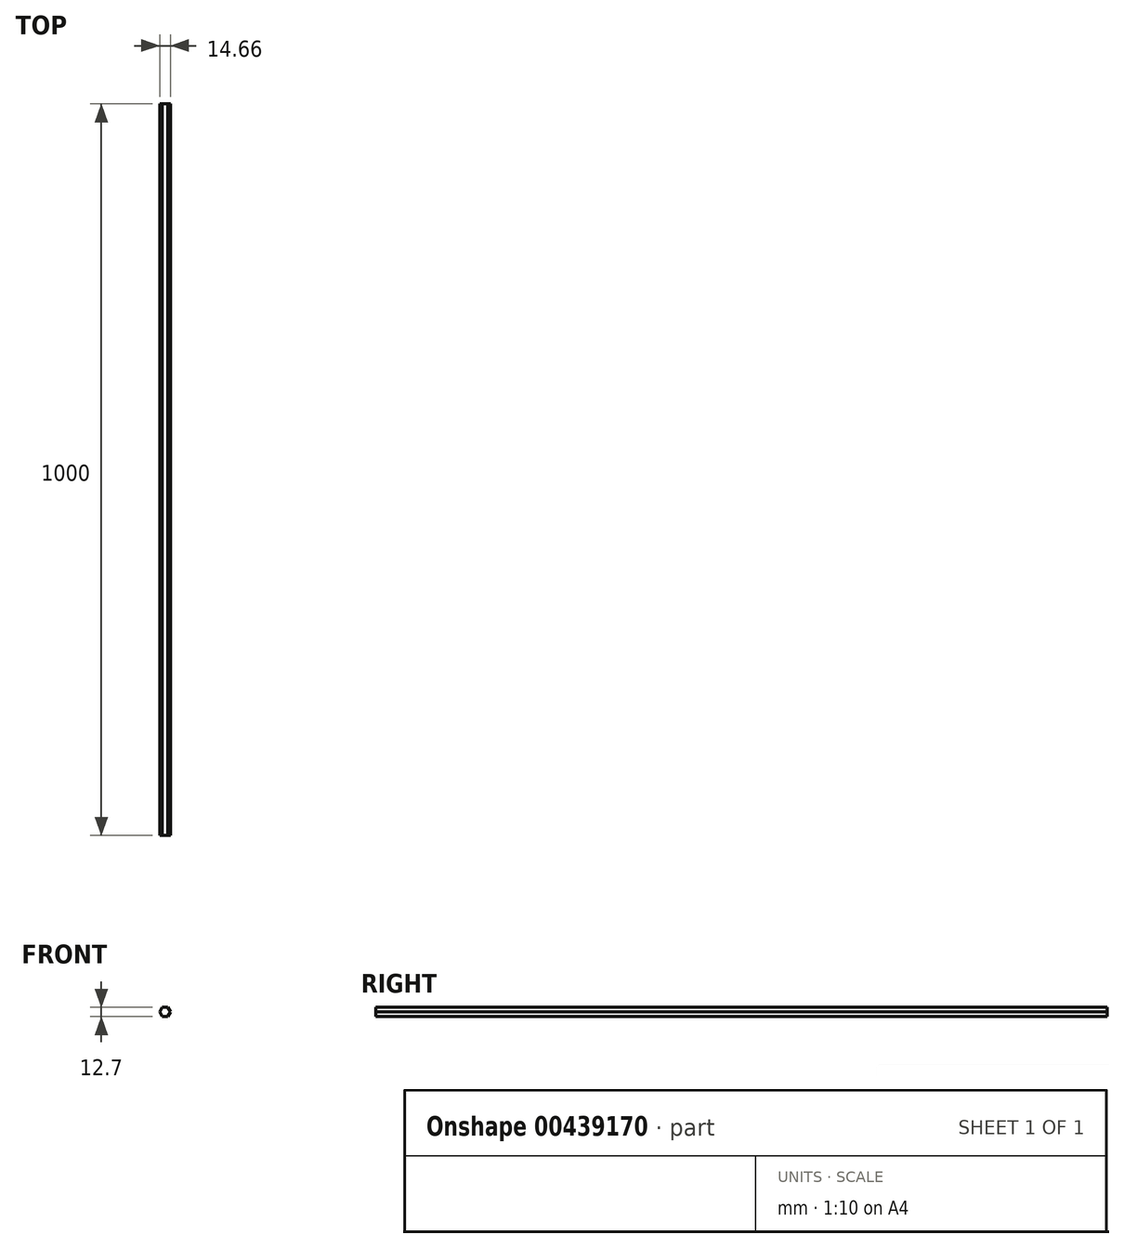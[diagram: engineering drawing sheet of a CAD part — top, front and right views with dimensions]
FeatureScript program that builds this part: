
annotation { "Feature Type Name" : "Feature", "Feature Type Description" : "" }
export const myFeature = defineFeature(function(context is Context, id is Id, definition is map)
    precondition{}
    {
        {
            var Q0;
            Q0=qCreatedBy(makeId("Front.planeOp"),FACE);
            var sketch = newSketch(context, id + "F0", { "sketchPlane" : qUnion([Q0])});
            skCircle(sketch, "E0.cCircle", {"center": v(0, 0) * mm, "radius": 6.35 * mm, "construction": true});
            skLineSegment(sketch, "E0.0", {"start": v(3.67, 6.35) * mm, "end": v(7.33, 0) * mm});
            skLineSegment(sketch, "E0.1", {"start": v(7.33, 0) * mm, "end": v(3.67, -6.35) * mm});
            skLineSegment(sketch, "E0.2", {"start": v(3.67, -6.35) * mm, "end": v(-3.67, -6.35) * mm});
            skLineSegment(sketch, "E0.3", {"start": v(-3.67, -6.35) * mm, "end": v(-7.33, 0) * mm});
            skLineSegment(sketch, "E0.4", {"start": v(-7.33, 0) * mm, "end": v(-3.67, 6.35) * mm});
            skLineSegment(sketch, "E0.5", {"start": v(-3.67, 6.35) * mm, "end": v(3.67, 6.35) * mm});
            skPoint(sketch, "E0.0.midPoint", {"position": v(5.5, 3.17) * mm});
            skSolve(sketch);
        }
        {
            var Q0;
            Q0=makeQuery(id+"F0.imprint","IMPRINT",FACE,{"disambiguationData":[TD([[makeQuery(id+"F0.imprint","IMPRINT",EDGE,{"derivedFrom":sQuery(id+"F0.wireOp",EDGE,"E0.0")}),-1.0]])]});
            extrude(context, id + "F1", {"entities" : qUnion([Q0]), "depth" : 1000 * mm});
        }
    });
